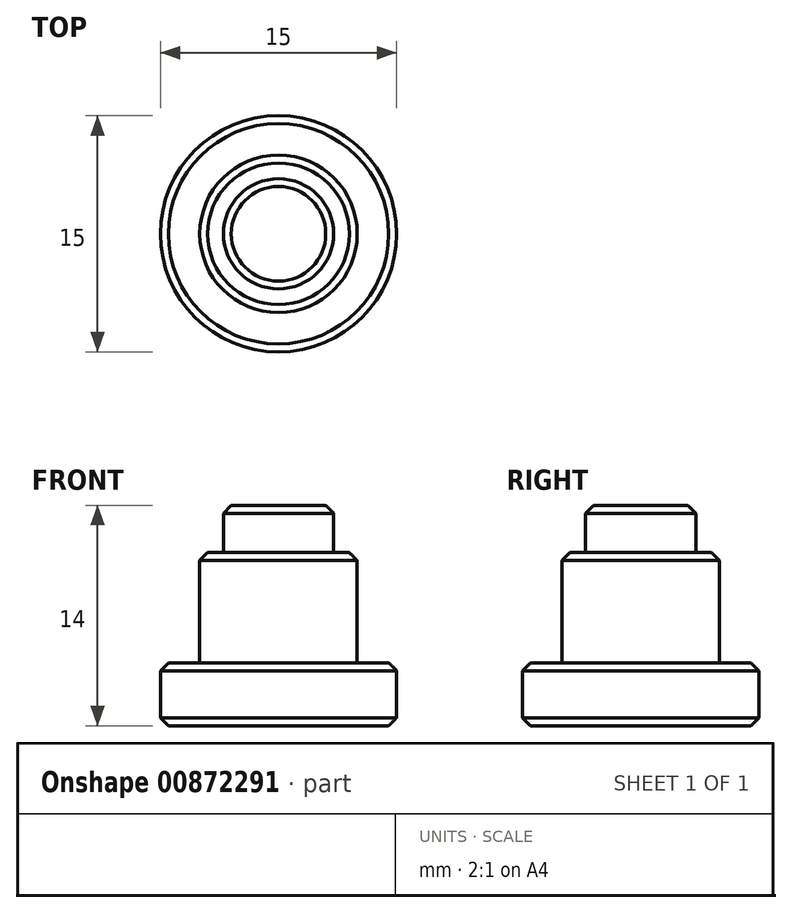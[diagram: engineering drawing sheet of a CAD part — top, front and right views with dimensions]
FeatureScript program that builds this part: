
annotation { "Feature Type Name" : "Feature", "Feature Type Description" : "" }
export const myFeature = defineFeature(function(context is Context, id is Id, definition is map)
    precondition{}
    {
        {
            var Q0;
            Q0=qCreatedBy(makeId("Top.planeOp"),FACE);
            var sketch = newSketch(context, id + "F0", { "sketchPlane" : qUnion([Q0])});
            skCircle(sketch, "E0", {"center": v(0, 0) * mm, "radius": 7.5 * mm});
            skSolve(sketch);
        }
        {
            var Q0;
            Q0=makeQuery(id+"F0.imprint","IMPRINT",FACE,{"disambiguationData":[TD([[makeQuery(id+"F0.imprint","IMPRINT",EDGE,{"derivedFrom":sQuery(id+"F0.wireOp",EDGE,"E0")}),1.0]])]});
            extrude(context, id + "F1", {"entities" : qUnion([Q0]), "depth" : 4 * mm, "offsetDistance" : 25 * mm});
        }
        {
            var Q0;
            Q0=makeQuery(id+"F1.opExtrude","CAP_FACE",FACE,{"disambiguationData":[OSD([sQuery(id+"F0.wireOp",EDGE,"E0")])],"isStart":false});
            var sketch = newSketch(context, id + "F2", { "sketchPlane" : qUnion([Q0])});
            skCircle(sketch, "E1", {"center": v(0, 0) * mm, "radius": 5 * mm});
            skSolve(sketch);
        }
        {
            var Q0;
            Q0 = qSketchRegion(id + "F2", true);
            extrude(context, id + "F3", {"entities" : qUnion([Q0]), "operationType" : NewBodyOperationType.ADD, "depth" : 7 * mm, "offsetDistance" : 25 * mm});
        }
        {
            var Q0;
            Q0=makeQuery(id+"F3.opExtrude","CAP_FACE",FACE,{"disambiguationData":[OSD([sQuery(id+"F2.wireOp",EDGE,"E1")])],"isStart":false});
            var sketch = newSketch(context, id + "F4", { "sketchPlane" : qUnion([Q0])});
            skCircle(sketch, "E2", {"center": v(0, 0) * mm, "radius": 3.5 * mm});
            skSolve(sketch);
        }
        {
            var Q0;
            Q0 = qSketchRegion(id + "F4", true);
            extrude(context, id + "F5", {"entities" : qUnion([Q0]), "operationType" : NewBodyOperationType.ADD, "depth" : 3 * mm, "offsetDistance" : 25 * mm});
        }
        {
            var Q0;
            Q0=makeQuery(id+"F5.opExtrude","CAP_EDGE",EDGE,{"disambiguationData":[OSD([sQuery(id+"F4.wireOp",EDGE,"E2")])],"isStart":false});
            var Q1;
            Q1=makeQuery(id+"F3.opExtrude","CAP_EDGE",EDGE,{"disambiguationData":[OSD([sQuery(id+"F2.wireOp",EDGE,"E1")])],"isStart":false});
            var Q2;
            Q2=makeQuery(id+"F1.opExtrude","CAP_EDGE",EDGE,{"disambiguationData":[OSD([sQuery(id+"F0.wireOp",EDGE,"E0")])],"isStart":false});
            var Q3;
            Q3=makeQuery(id+"F1.opExtrude","CAP_EDGE",EDGE,{"disambiguationData":[OSD([sQuery(id+"F0.wireOp",EDGE,"E0")])],"isStart":true});
            chamfer(context, id + "F6", {"entities" : qUnion([Q0, Q1, Q2, Q3]), "width" : .5 * mm, "tangentPropagation" : true});
        }
    });
